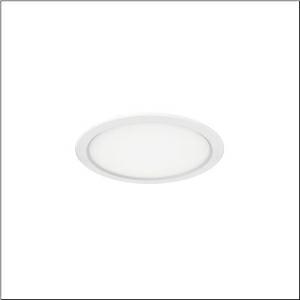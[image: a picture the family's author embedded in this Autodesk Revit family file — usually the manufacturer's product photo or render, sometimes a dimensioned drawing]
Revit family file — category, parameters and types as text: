
# Revit family: lunis_41_eco_51ds107f34b
name_source: partatom
category: Lighting Fixtures
units: mm (PartAtom-declared; Revit-internal decimal feet)

## family parameters
Cut with Voids When Loaded = No
Host = Face
Light Source = No
Part Type = Normal
Room Calculation Point = No
Round Connector Dimension = Use Diameter
Shared = No

## types (1)
- Lunis 41 Eco (1 x LED, 2150 lm, 17.5 W, 3000K)
    Apparent Load = 18 VA
    CIE Flux Codes = 47 80 97 100 100
    Color Rendering = 80
    Color Temperature = 3000K
    Default Elevation = 1800 mm
    Description = Lunis 41,  Eco, downlight, light emission: direct distribution, LED rated luminous flux: 2.150lm, light colour: 830, mains connection: 230V, AC, 50/60Hz, housing, round, of aluminium, coated, traffic white (RAL 9016), diameter: 216mm, recess depth: 58mm, protection rating (complete): IP20, protection rating (on room side): IP40, insulation class (complete): insulation class II (safety insulation), certification: CE, permissible ambient temperature for indoor applications: -20..+40°C, packaging unit: 1 piece
    Height = 0 mm  [stored 0 ft]
    Lamp = 1 x LED
    Lamp Light Flux = 2150 lm
    Lamp Power = 17.5 W
    Lamp count = 1
    Length = 216 mm
    Luminous efficacy = 123 lm/W
    Manufacturer = Siteco
    ModVariant = No
    Model = 51DS107F34B
    Mounting Place = Ceiling
    Mounting Type = Recessed
    Number of Poles = 1
    OnlyDefault = Yes
    Power Factor = 1
    Product Name = Lunis 41 Eco
    Product group = downlight
    ProductGroupID = 400
    Protection Class = Protection class II
    Protection Degree = IP 20
    RLX_Detail_Level = 1
    RLX_Emergency_Light_Flux = 0 lm
    RLX_Emergency_Type = 0
    RLX_Emergency_Type_DB = No
    RlxData = <blob elided: 10229 chars, md5=74c88c6a>
    Socket = socket
    Standby Power = 0 W
    System Light Flux = 2150 lm
    System Power = 18 W
    Type Comments = Product without accessories
    Type Image = l_1345914.jpg
    URL = http://relux.com
    VarID = ---
    Voltage = 0 V
    Weight = 0.00 kg
    Width = 0 mm  [stored 0 ft]

note: [stored X ft] marks values corroborated as IEEE doubles in the binary element streams (Revit-internal decimal feet)

## geometry (parser evidence)
native form markers: Sweep x10
no freeform markers — native parametric forms only
